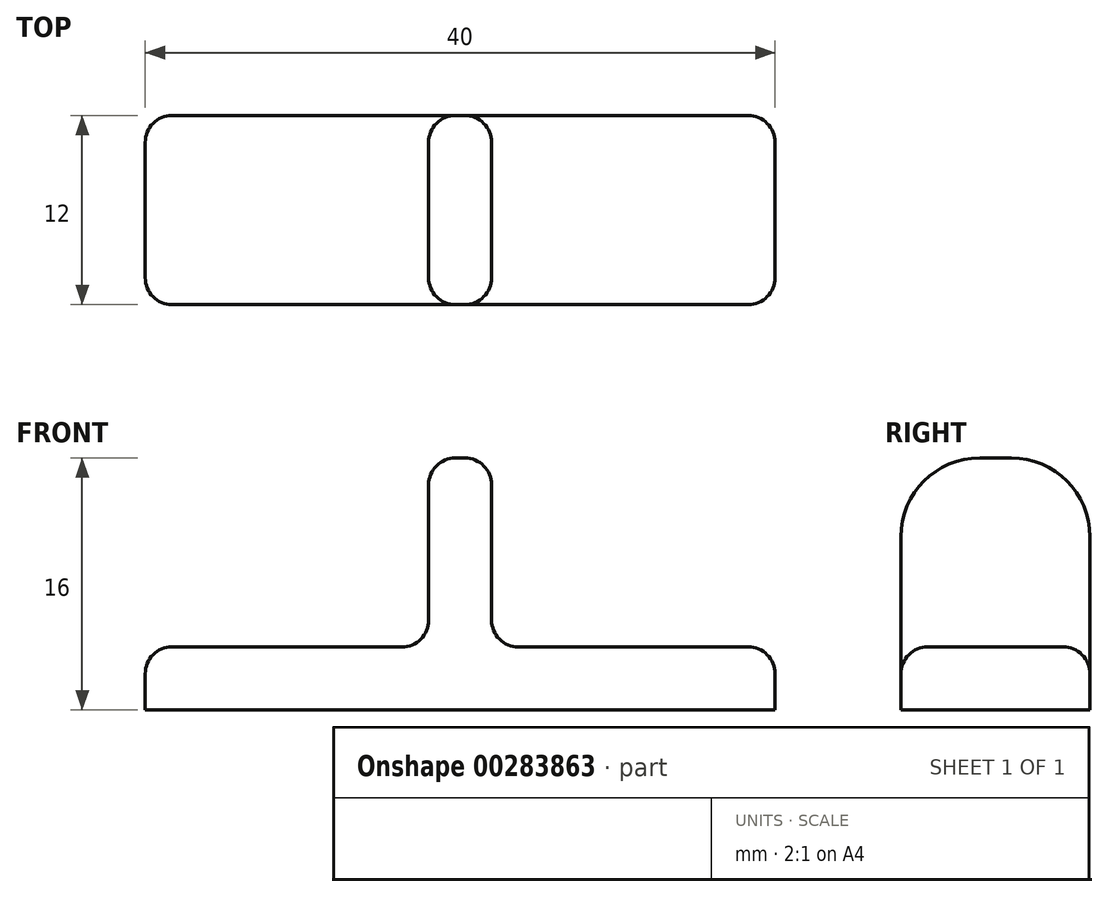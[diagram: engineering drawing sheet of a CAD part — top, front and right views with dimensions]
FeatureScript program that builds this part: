
annotation { "Feature Type Name" : "Feature", "Feature Type Description" : "" }
export const myFeature = defineFeature(function(context is Context, id is Id, definition is map)
    precondition{}
    {
        {
            var Q0;
            Q0=qCreatedBy(makeId("Top.planeOp"),FACE);
            var sketch = newSketch(context, id + "F0", { "sketchPlane" : qUnion([Q0])});
            skLineSegment(sketch, "E0.bottom", {"start": v(-20, 6) * mm, "end": v(20, 6) * mm});
            skLineSegment(sketch, "E0.top", {"start": v(-20, -6) * mm, "end": v(20, -6) * mm});
            skLineSegment(sketch, "E0.left", {"start": v(-20, 6) * mm, "end": v(-20, -6) * mm});
            skLineSegment(sketch, "E0.right", {"start": v(20, 6) * mm, "end": v(20, -6) * mm});
            skSolve(sketch);
        }
        {
            var Q0;
            Q0=makeQuery(id+"F0.imprint","IMPRINT",FACE,{"disambiguationData":[TD([[makeQuery(id+"F0.imprint","IMPRINT",EDGE,{"derivedFrom":sQuery(id+"F0.wireOp",EDGE,"E0.bottom")}),-1.0]])]});
            extrude(context, id + "F1", {"entities" : qUnion([Q0]), "depth" : 4 * mm});
        }
        {
            var Q0;
            Q0=makeQuery(id+"F1.opExtrude","CAP_FACE",FACE,{"disambiguationData":[OSD([sQuery(id+"F0.wireOp",EDGE,"E0.bottom"),sQuery(id+"F0.wireOp",EDGE,"E0.top"),sQuery(id+"F0.wireOp",EDGE,"E0.left"),sQuery(id+"F0.wireOp",EDGE,"E0.right")])],"isStart":false});
            var sketch = newSketch(context, id + "F2", { "sketchPlane" : qUnion([Q0])});
            skLineSegment(sketch, "E1.bottom", {"start": v(-2, 6) * mm, "end": v(2, 6) * mm});
            skLineSegment(sketch, "E1.top", {"start": v(-2, -6) * mm, "end": v(2, -6) * mm});
            skLineSegment(sketch, "E1.left", {"start": v(-2, 6) * mm, "end": v(-2, -6) * mm});
            skLineSegment(sketch, "E1.right", {"start": v(2, 6) * mm, "end": v(2, -6) * mm});
            skSolve(sketch);
        }
        {
            var Q0;
            Q0=makeQuery(id+"F2.imprint","IMPRINT",FACE,{"disambiguationData":[TD([[makeQuery(id+"F2.imprint","IMPRINT",EDGE,{"derivedFrom":sQuery(id+"F2.wireOp",EDGE,"E1.bottom")}),-1.0]])]});
            extrude(context, id + "F3", {"entities" : qUnion([Q0]), "operationType" : NewBodyOperationType.ADD, "depth" : 12 * mm});
        }
        {
            var Q0;
            Q0=makeQuery(id+"F3.opExtrude","CAP_EDGE",EDGE,{"disambiguationData":[OSD([sQuery(id+"F2.wireOp",EDGE,"E1.top")])],"isStart":false});
            var Q1;
            Q1=makeQuery(id+"F3.opExtrude","CAP_EDGE",EDGE,{"disambiguationData":[OSD([sQuery(id+"F2.wireOp",EDGE,"E1.bottom")])],"isStart":false});
            fillet(context, id + "F4", {"entities" : qUnion([Q0, Q1]), "radius" : 5 * mm, "tangentPropagation" : true, "allowEdgeOverflow" : false});
        }
        {
            var Q0;
            Q0=makeQuery(id+"F1.opExtrude","SWEPT_EDGE",EDGE,{"disambiguationData":[OSD([sQuery(id+"F0.wireOp",EDGE,"E0.top"),sQuery(id+"F0.wireOp",EDGE,"E0.left")])]});
            var Q1;
            {var subQ0=sQuery(id+"F0.wireOp",EDGE,"E0.left");var subQ1=sQuery(id+"F0.wireOp",EDGE,"E0.top");Q1=makeQuery(id+"F3.boolean.opBoolean","SPLIT",EDGE,{"disambiguationData":[TD([makeQuery(id+"F1.opExtrude","SWEPT_FACE",FACE,{"disambiguationData":[OSD([subQ0])]})])],"derivedFrom":makeQuery(id+"F1.opExtrude","CAP_EDGE",EDGE,{"disambiguationData":[OSD([subQ1])],"isStart":false})});}
            var Q2;
            Q2=makeQuery(id+"F1.opExtrude","CAP_EDGE",EDGE,{"disambiguationData":[OSD([sQuery(id+"F0.wireOp",EDGE,"E0.left")])],"isStart":false});
            var Q3;
            Q3=makeQuery(id+"F1.opExtrude","SWEPT_EDGE",EDGE,{"disambiguationData":[OSD([sQuery(id+"F0.wireOp",EDGE,"E0.bottom"),sQuery(id+"F0.wireOp",EDGE,"E0.left")])]});
            var Q4;
            {var subQ0=sQuery(id+"F0.wireOp",EDGE,"E0.left");var subQ1=sQuery(id+"F0.wireOp",EDGE,"E0.bottom");Q4=makeQuery(id+"F3.boolean.opBoolean","SPLIT",EDGE,{"disambiguationData":[TD([makeQuery(id+"F1.opExtrude","SWEPT_FACE",FACE,{"disambiguationData":[OSD([subQ0])]})])],"derivedFrom":makeQuery(id+"F1.opExtrude","CAP_EDGE",EDGE,{"disambiguationData":[OSD([subQ1])],"isStart":false})});}
            var Q5;
            Q5=makeQuery(id+"F1.opExtrude","SWEPT_EDGE",EDGE,{"disambiguationData":[OSD([sQuery(id+"F0.wireOp",EDGE,"E0.top"),sQuery(id+"F0.wireOp",EDGE,"E0.right")])]});
            var Q6;
            Q6=makeQuery(id+"F1.opExtrude","SWEPT_EDGE",EDGE,{"disambiguationData":[OSD([sQuery(id+"F0.wireOp",EDGE,"E0.bottom"),sQuery(id+"F0.wireOp",EDGE,"E0.right")])]});
            var Q7;
            {var subQ0=sQuery(id+"F0.wireOp",EDGE,"E0.right");var subQ1=sQuery(id+"F0.wireOp",EDGE,"E0.top");Q7=makeQuery(id+"F3.boolean.opBoolean","SPLIT",EDGE,{"disambiguationData":[TD([makeQuery(id+"F1.opExtrude","SWEPT_FACE",FACE,{"disambiguationData":[OSD([subQ0])]})])],"derivedFrom":makeQuery(id+"F1.opExtrude","CAP_EDGE",EDGE,{"disambiguationData":[OSD([subQ1])],"isStart":false})});}
            var Q8;
            Q8=makeQuery(id+"F1.opExtrude","CAP_EDGE",EDGE,{"disambiguationData":[OSD([sQuery(id+"F0.wireOp",EDGE,"E0.right")])],"isStart":false});
            var Q9;
            {var subQ0=sQuery(id+"F0.wireOp",EDGE,"E0.right");var subQ1=sQuery(id+"F0.wireOp",EDGE,"E0.bottom");Q9=makeQuery(id+"F3.boolean.opBoolean","SPLIT",EDGE,{"disambiguationData":[TD([makeQuery(id+"F1.opExtrude","SWEPT_FACE",FACE,{"disambiguationData":[OSD([subQ0])]})])],"derivedFrom":makeQuery(id+"F1.opExtrude","CAP_EDGE",EDGE,{"disambiguationData":[OSD([subQ1])],"isStart":false})});}
            var Q10;
            Q10=makeQuery(id+"F3.opExtrude","SWEPT_FACE",FACE,{"disambiguationData":[OSD([sQuery(id+"F2.wireOp",EDGE,"E1.left")])]});
            var Q11;
            {var subQ0=sQuery(id+"F0.wireOp",EDGE,"E0.left");var subQ1=sQuery(id+"F0.wireOp",EDGE,"E0.top");var subQ2=sQuery(id+"F0.wireOp",EDGE,"E0.bottom");Q11=makeQuery(id+"F3.boolean.opBoolean","SPLIT",FACE,{"disambiguationData":[TD([makeQuery(id+"F1.opExtrude","SWEPT_FACE",FACE,{"disambiguationData":[OSD([subQ0])]})])],"derivedFrom":makeQuery(id+"F1.opExtrude","CAP_FACE",FACE,{"disambiguationData":[OSD([subQ2,subQ1,subQ0,sQuery(id+"F0.wireOp",EDGE,"E0.right")])],"isStart":false})});}
            var Q12;
            Q12=makeQuery(id+"F3.opExtrude","CAP_EDGE",EDGE,{"disambiguationData":[OSD([sQuery(id+"F2.wireOp",EDGE,"E1.left")])],"isStart":true});
            var Q13;
            Q13=makeQuery(id+"F3.opExtrude","SWEPT_EDGE",EDGE,{"disambiguationData":[OSD([sQuery(id+"F0.wireOp",EDGE,"E0.top"),sQuery(id+"F2.wireOp",EDGE,"E1.top"),sQuery(id+"F2.wireOp",EDGE,"E1.right")])]});
            var Q14;
            Q14=makeQuery(id+"F3.opExtrude","SWEPT_EDGE",EDGE,{"disambiguationData":[OSD([sQuery(id+"F0.wireOp",EDGE,"E0.bottom"),sQuery(id+"F2.wireOp",EDGE,"E1.bottom"),sQuery(id+"F2.wireOp",EDGE,"E1.right")])]});
            var Q15;
            Q15=makeQuery(id+"F4.opFillet","BLEND_EDGE",EDGE,{"blendedFrom":[makeQuery(id+"F3.opExtrude","CAP_EDGE",EDGE,{"disambiguationData":[OSD([sQuery(id+"F2.wireOp",EDGE,"E1.bottom")])],"isStart":false}),makeQuery(id+"F3.opExtrude","SWEPT_FACE",FACE,{"disambiguationData":[OSD([sQuery(id+"F2.wireOp",EDGE,"E1.right")])]})],"blendedInto":[makeQuery(id+"F3.opExtrude","SWEPT_FACE",FACE,{"disambiguationData":[OSD([sQuery(id+"F2.wireOp",EDGE,"E1.right")])]})]});
            var Q16;
            Q16=makeQuery(id+"F3.opExtrude","CAP_EDGE",EDGE,{"disambiguationData":[OSD([sQuery(id+"F2.wireOp",EDGE,"E1.right")])],"isStart":false});
            var Q17;
            Q17=makeQuery(id+"F3.opExtrude","CAP_EDGE",EDGE,{"disambiguationData":[OSD([sQuery(id+"F2.wireOp",EDGE,"E1.right")])],"isStart":true});
            fillet(context, id + "F5", {"entities" : qUnion([Q0, Q1, Q2, Q3, Q4, Q5, Q6, Q7, Q8, Q9, Q10, Q11, Q12, Q13, Q14, Q15, Q16, Q17]), "radius" : 1.7 * mm, "allowEdgeOverflow" : false});
        }
    });
